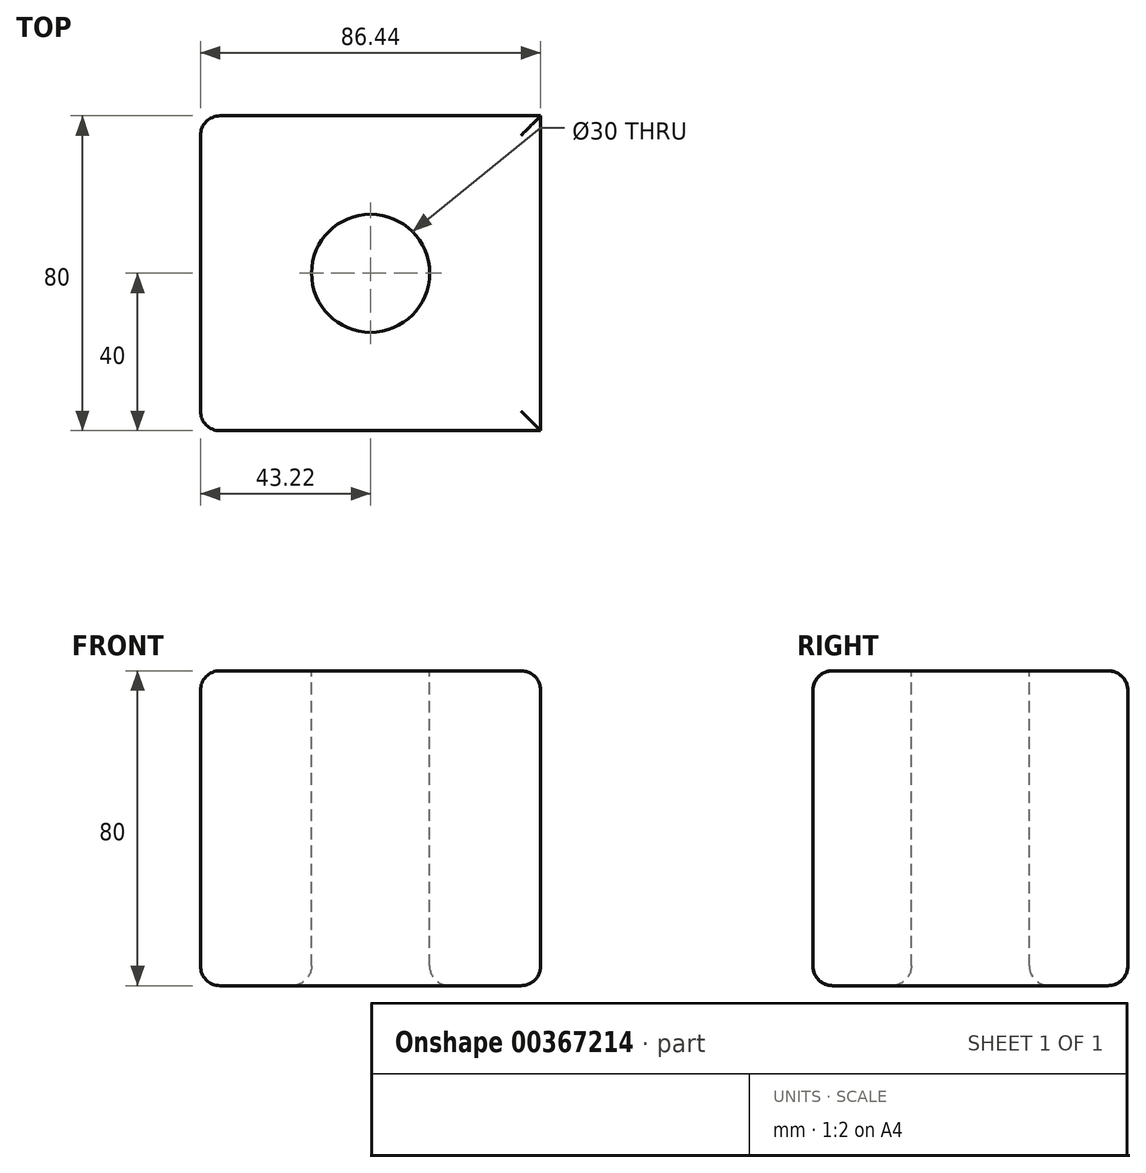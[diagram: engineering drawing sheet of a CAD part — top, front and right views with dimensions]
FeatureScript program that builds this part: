
annotation { "Feature Type Name" : "Feature", "Feature Type Description" : "" }
export const myFeature = defineFeature(function(context is Context, id is Id, definition is map)
    precondition{}
    {
        {
            var Q0;
            Q0=qCreatedBy(makeId("Top.planeOp"),FACE);
            var sketch = newSketch(context, id + "F0", { "sketchPlane" : qUnion([Q0])});
            skLineSegment(sketch, "E0.bottom", {"start": v(-43.22, 40) * mm, "end": v(43.22, 40) * mm});
            skLineSegment(sketch, "E0.top", {"start": v(-43.22, -40) * mm, "end": v(43.22, -40) * mm});
            skLineSegment(sketch, "E0.left", {"start": v(-43.22, 40) * mm, "end": v(-43.22, -40) * mm});
            skLineSegment(sketch, "E0.right", {"start": v(43.22, 40) * mm, "end": v(43.22, -40) * mm});
            skPoint(sketch, "E0.middle", {"position": v(0, 0) * mm});
            skSolve(sketch);
        }
        {
            var Q0;
            Q0=makeQuery(id+"F0.imprint","IMPRINT",FACE,{"disambiguationData":[TD([[makeQuery(id+"F0.imprint","IMPRINT",EDGE,{"derivedFrom":sQuery(id+"F0.wireOp",EDGE,"E0.bottom")}),-1.0]])]});
            extrude(context, id + "F1", {"entities" : qUnion([Q0]), "depth" : 80 * mm});
        }
        {
            var Q0;
            Q0=makeQuery(id+"F1.opExtrude","CAP_FACE",FACE,{"disambiguationData":[OSD([sQuery(id+"F0.wireOp",EDGE,"E0.bottom"),sQuery(id+"F0.wireOp",EDGE,"E0.top"),sQuery(id+"F0.wireOp",EDGE,"E0.left"),sQuery(id+"F0.wireOp",EDGE,"E0.right")])],"isStart":false});
            var sketch = newSketch(context, id + "F2", { "sketchPlane" : qUnion([Q0])});
            skCircle(sketch, "E1", {"center": v(0, 0) * mm, "radius": 15 * mm});
            skSolve(sketch);
        }
        {
            var Q0;
            Q0=makeQuery(id+"F2.imprint","IMPRINT",FACE,{"disambiguationData":[TD([[makeQuery(id+"F2.imprint","IMPRINT",EDGE,{"derivedFrom":sQuery(id+"F2.wireOp",EDGE,"E1")}),1.0]])]});
            extrude(context, id + "F3", {"entities" : qUnion([Q0]), "operationType" : NewBodyOperationType.REMOVE, "endBound" : BoundingType.THROUGH_ALL, "oppositeDirection" : true, "depth" : 25 * mm});
        }
        {
            var Q0;
            Q0=makeQuery(id+"F1.opExtrude","SWEPT_EDGE",EDGE,{"disambiguationData":[OSD([sQuery(id+"F0.wireOp",EDGE,"E0.top"),sQuery(id+"F0.wireOp",EDGE,"E0.left")])]});
            var Q1;
            Q1=makeQuery(id+"F1.opExtrude","CAP_EDGE",EDGE,{"disambiguationData":[OSD([sQuery(id+"F0.wireOp",EDGE,"E0.left")])],"isStart":true});
            var Q2;
            Q2=makeQuery(id+"F1.opExtrude","SWEPT_EDGE",EDGE,{"disambiguationData":[OSD([sQuery(id+"F0.wireOp",EDGE,"E0.bottom"),sQuery(id+"F0.wireOp",EDGE,"E0.left")])]});
            var Q3;
            Q3=makeQuery(id+"F1.opExtrude","CAP_EDGE",EDGE,{"disambiguationData":[OSD([sQuery(id+"F0.wireOp",EDGE,"E0.top")])],"isStart":true});
            var Q4;
            Q4=makeQuery(id+"F1.opExtrude","CAP_EDGE",EDGE,{"disambiguationData":[OSD([sQuery(id+"F0.wireOp",EDGE,"E0.bottom")])],"isStart":true});
            var Q5;
            Q5=makeQuery(id+"F1.opExtrude","CAP_EDGE",EDGE,{"disambiguationData":[OSD([sQuery(id+"F0.wireOp",EDGE,"E0.right")])],"isStart":true});
            var Q6;
            Q6=makeQuery(id+"F1.opExtrude","CAP_EDGE",EDGE,{"disambiguationData":[OSD([sQuery(id+"F0.wireOp",EDGE,"E0.bottom")])],"isStart":false});
            var Q7;
            Q7=makeQuery(id+"F1.opExtrude","CAP_EDGE",EDGE,{"disambiguationData":[OSD([sQuery(id+"F0.wireOp",EDGE,"E0.left")])],"isStart":false});
            var Q8;
            Q8=makeQuery(id+"F1.opExtrude","CAP_EDGE",EDGE,{"disambiguationData":[OSD([sQuery(id+"F0.wireOp",EDGE,"E0.top")])],"isStart":false});
            var Q9;
            Q9=makeQuery(id+"F1.opExtrude","CAP_EDGE",EDGE,{"disambiguationData":[OSD([sQuery(id+"F0.wireOp",EDGE,"E0.right")])],"isStart":false});
            var Q10;
            Q10=makeQuery(id+"F3.boolean.opBoolean","COPY",EDGE,{"derivedFrom":makeQuery(id+"F3.opExtrude","CAP_EDGE",EDGE,{"disambiguationData":[OSD([sQuery(id+"F2.wireOp",EDGE,"E1")])],"isStart":true})});
            var Q11;
            Q11=makeQuery(id+"F3.boolean.opBoolean","INTERSECT",EDGE,{"derivedFrom":[makeQuery(id+"F1.opExtrude","CAP_FACE",FACE,{"disambiguationData":[OSD([sQuery(id+"F0.wireOp",EDGE,"E0.bottom"),sQuery(id+"F0.wireOp",EDGE,"E0.top"),sQuery(id+"F0.wireOp",EDGE,"E0.left"),sQuery(id+"F0.wireOp",EDGE,"E0.right")])],"isStart":true}),makeQuery(id+"F3.opExtrude","SWEPT_FACE",FACE,{"disambiguationData":[OSD([sQuery(id+"F2.wireOp",EDGE,"E1")])]})]});
            fillet(context, id + "F4", {"entities" : qUnion([Q0, Q1, Q2, Q3, Q4, Q5, Q6, Q7, Q8, Q9, Q10, Q11]), "radius" : 5 * mm, "tangentPropagation" : true, "allowEdgeOverflow" : false});
        }
    });
